# Revit family: Блоки пассивные_АРИЯ
name_source: partatom
category: Системы пожарной сигнализации
revit_build: Autodesk Revit MEP 2016 (Build: 20150220_1215(x64)
units: mm (PartAtom-declared; Revit-internal decimal feet)

## family parameters
Общий = Нет
Основа = Грань
При загрузке вырезать с полостями = Нет
Размер круглого соединителя = Использовать диаметр
Сохранять ориентацию аннотаций = Нет
Тип детали = Нормальный
Точка расчета площади = Нет

## types (6) — shared parameters
ADSK_URL документации изделия = https://omelta.com
ADSK_URL страницы изделия = https://omelta.com
ADSK_Единица измерения = шт.
ADSK_Завод-изготовитель = г. Омск, ООО «Электротехника и Автоматика»
ADSK_Код изделия = 437245
ADSK_Размер_Высота = 245 мм
ADSK_Размер_Глубина = 90 мм
ADSK_Размер_Ширина = 200 мм
Выходная мощность = 40 Вт
Гарантийный срок службы = 5 лет
Диапазон рабочих температур = –10...+55 °С
Количество зон = 1
Материал_Корпус = ЭиА_Черный
Материал_Надпись = ЭиА_Белый
zero-valued in all types: Отметка по умолчанию

## per-type parameters (varying)
| type | ADSK_Масса | ADSK_Наименование | ADSK_Напряжение | ADSK_Номинальная мощность | ADSK_Обозначение | ADSK_Ток | IP | Надпись |
| АРИЯ-ПС-БРО-РМ | 0.9 | Блок речевого оповещения | 220 В | 7 В·А | Блок речевого оповещения пассивный однозональный с резервным источником питания и возможностью трансляции музыки | 31 мА | 40 | АРИЯ-ПС-
БРО-РМ |
| АРИЯ-ПС-БР-РМ | 0.82 | Блок расширения | 220 В | 7 В·А | Блок расширения пассивный однозональный с резервным источником питания и возможностью трансляции музыки | 31 мА | 40 | АРИЯ-ПС-
БР-РМ |
| АРИЯ-ПС-БРО-Р | 0.85 | Блок речевого оповещения | 220 В | 3 В·А | Блок речевого оповещения пассивный однозональный с резервным источником питания | 13 мА | 40 | АРИЯ-ПС-
БРО-Р |
| АРИЯ-ПС-БР-Р | 0.8 | Блок расширения | 220 В | 3 В·А | Блок расширения пассивный однозональный с резервным источником питания | 13 мА | 40 | АРИЯ-ПС-
БР-Р |
| АРИЯ-ПС-БРО-М | 0.7 | Блок речевого оповещения | 12 В | 6 В·А | Блок речевого оповещения пассивный однозональный с возможностью трансляции музыки | 500 мА | 41 | АРИЯ-ПС-
БРО-М |
| АРИЯ-ПС-БР-М | 0.6 | Блок расширения | 12 В | 6 В·А | Блок расширения пассивный однозональный с возможностью трансляции музыки | 500 мА | 41 | АРИЯ-ПС-
БР-М |

note: column(s) folded — value = type name in every type: ADSK_Марка

## geometry (parser evidence)
native form markers: Blend x2
no freeform markers — native parametric forms only
